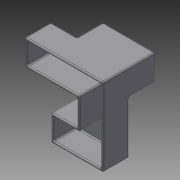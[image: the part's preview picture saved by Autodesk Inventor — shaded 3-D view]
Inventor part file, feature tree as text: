
AUTODESK INVENTOR PART (.ipt)
format: ipt  version: 2014 (Build 180170000, 170)  size: 206,336 bytes
history: native  units: in
note: dims shown in document units (in); Inventor stores cm internally (conversion verified against a paired STEP export)
features: plane x8, extrude x2, other x1, shell x1, fillet x1, sketch x1
ambient origin geometry x8: Origin, YZ Plane, XZ Plane, XY Plane, X Axis, Y Axis, Z Axis, Center Point
bodies: Solid1 (feature_tree)
feature tree (14):
  other  "Cube Master.ipt"
  extrude  "Extrusion1"  Depth=0.3937in
  extrude  "Extrusion2"  Depth=0.0193in TaperAngle=0.0deg
  shell  "Shell1"  Thickness=1.0in
  fillet  "Fillet1"  Radius=0.0394in
  sketch  "Sketch1"  dims[d0=0.3937in d1=0.3937in d2=1.0in d3=0.0in d4=1.0in d5=0.0in d6=0.0394in d7=0.0193in d8=0.0193in]
  plane  "Work Plane1"
  plane  "Work Plane2"
  plane  "Work Plane3"
  plane  "Work Plane4"
  plane  "Work Plane5"
  plane  "Work Plane6"
  plane  "Work Plane7"
  plane  "Work Plane8"
